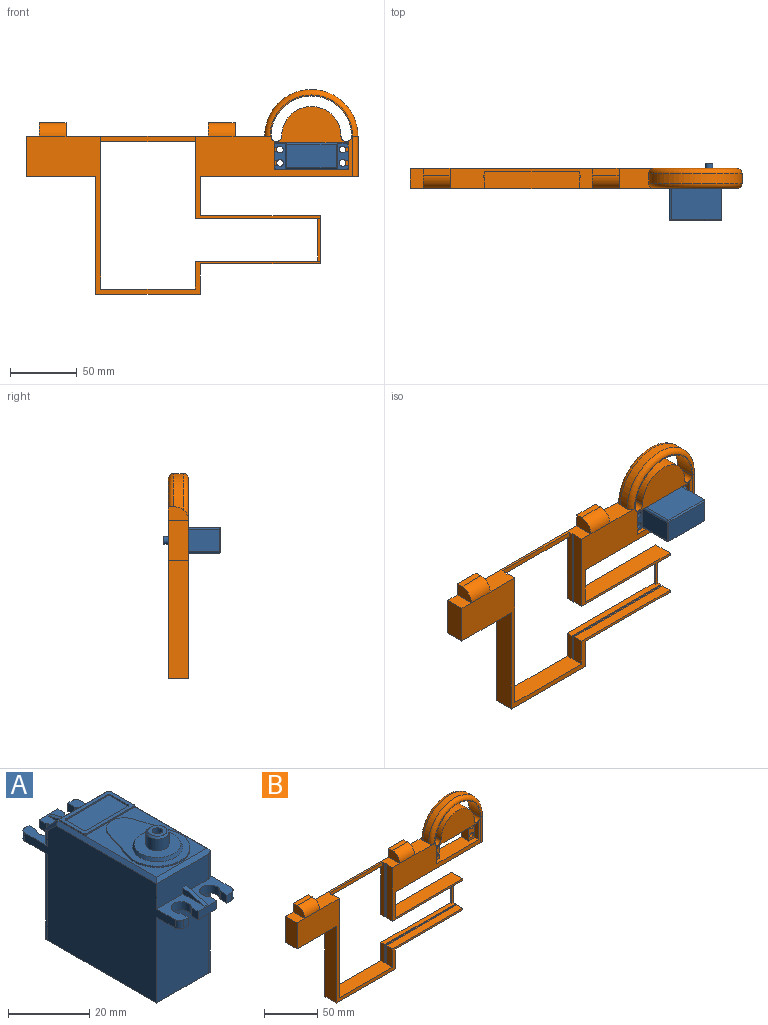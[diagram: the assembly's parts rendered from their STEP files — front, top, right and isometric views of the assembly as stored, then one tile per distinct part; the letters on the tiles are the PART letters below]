
ASSEMBLY  parts=2 mates=1
PART A: 88 faces, bbox 19.5x55.4x43.3 mm
  f0: plane 25.45x17.5mm, normal (0,0,1), area 153.9mm2, adj f42,f43,f44,f45,f56,f57,f58,f77
  f1: plane 17.5x0.91mm, normal (0,0,1), area 7.4mm2, adj f41,f56,f58,f71,f84,f85
  f2: plane 19.5x9.5mm, normal (0,0,1), area 94.3mm2, adj f3,f4,f5,f14,f15,f29,f30,f31
  f3: plane 16.5x3.98mm, normal (0,1,0), area 63.2mm2, adj f2,f36,f37,f38,f60,f61,f62
  f4: plane 2.45x1.5mm, normal (0,1,0), area 3.7mm2, adj f2,f6,f34,f40
  f5: plane 6.5x2.45mm, normal (0,1,0), area 15.9mm2, adj f2,f6,f30,f33
  f6: plane 19.5x9.5mm, normal (0,0,-1), area 103.3mm2, adj f4,f5,f7,f14,f15,f29,f30,f31
  f7: plane 25.85x16.5mm, normal (0,1,0), area 426.5mm2, adj f6,f52,f64,f65
  f8: plane 19.5x9.5mm, normal (0,0,1), area 93.8mm2, adj f9,f10,f11,f14,f15,f17,f18,f19
  f9: plane 18x7.6mm, normal (0,-1,0), area 134.4mm2, adj f8,f14,f24,f25,f26,f57,f63
  f10: plane 6.5x2.45mm, normal (0,-1,0), area 15.9mm2, adj f8,f12,f18,f23
  f11: plane 2.45x1.5mm, normal (0,-1,0), area 3.7mm2, adj f8,f12,f20,f27
  f12: plane 19.5x9.5mm, normal (0,0,-1), area 102.8mm2, adj f10,f11,f13,f14,f15,f17,f18,f19
  f13: plane 25.85x18mm, normal (0,-1,0), area 465.3mm2, adj f12,f14,f53,f66
  f14: plane 52.4x35.9mm, normal (-1,0,0), area 1391.9mm2, adj f2,f6,f8,f9,f12,f13,f27,f39
  f15: plane 52.4x35.9mm, normal (1,0,0), area 1341.7mm2, adj f2,f6,f8,f12,f28,f40,f54,f58
  f16: plane 37.4x17.5mm, normal (0,0,-1), area 654.5mm2, adj f51,f52,f53,f54
  f17: plane 2.45x1.5mm, normal (0,-1,0), area 3.7mm2, adj f8,f12,f21,f28
  f18: plane 2.45x2.41mm, normal (-1,0,0), area 5.9mm2, adj f8,f10,f12,f19
  f19: cylinder r=2.5mm len=5mm, axis (0,0,1), area 29mm2, adj f8,f12,f18,f20
  f20: plane 2.45x2.41mm, normal (1,0,0), area 5.9mm2, adj f8,f11,f12,f19
  f21: plane 2.45x2.41mm, normal (-1,0,0), area 5.9mm2, adj f8,f12,f17,f22
  f22: cylinder r=2.5mm len=5mm, axis (0,0,1), area 29mm2, adj f8,f12,f21,f23
  f23: plane 2.45x2.41mm, normal (1,0,0), area 5.9mm2, adj f8,f10,f12,f22
  f24: plane 7.5x2mm, normal (0,-0.26,0.97), area 9.3mm2, adj f8,f9,f25,f26
  f25: plane 7.5x2mm, normal (1,0,0), area 7.5mm2, adj f8,f9,f24
  f26: plane 7.5x2mm, normal (-1,0,0), area 7.5mm2, adj f8,f9,f24
  f27: cylinder r=1.5mm len=2.45mm, axis (0,0,1), area 5.8mm2, adj f8,f11,f12,f14
  f28: cylinder r=1.5mm len=2.45mm, axis (0,0,-1), area 5.8mm2, adj f8,f12,f15,f17
  f29: plane 2.45x1.5mm, normal (0,1,0), area 3.7mm2, adj f2,f6,f31,f39
  f30: plane 2.45x2.41mm, normal (-1,0,0), area 5.9mm2, adj f2,f5,f6,f32
  f31: plane 2.45x2.41mm, normal (1,0,0), area 5.9mm2, adj f2,f6,f29,f32
  f32: cylinder r=2.5mm len=5mm, axis (0,0,1), area 29mm2, adj f2,f6,f30,f31
  f33: plane 2.45x2.41mm, normal (1,0,0), area 5.9mm2, adj f2,f5,f6,f35
  f34: plane 2.45x2.41mm, normal (-1,0,0), area 5.9mm2, adj f2,f4,f6,f35
  f35: cylinder r=2.5mm len=5mm, axis (0,0,1), area 29mm2, adj f2,f6,f33,f34
  f36: plane 7.5x2mm, normal (0,0.26,0.97), area 9.3mm2, adj f2,f3,f37,f38
  f37: plane 7.5x2mm, normal (1,0,0), area 7.5mm2, adj f2,f3,f36
  f38: plane 7.5x2mm, normal (-1,0,0), area 7.5mm2, adj f2,f3,f36
  f39: cylinder r=1.5mm len=2.45mm, axis (0,0,1), area 5.8mm2, adj f2,f6,f14,f29
  f40: cylinder r=1.5mm len=2.45mm, axis (0,0,-1), area 5.8mm2, adj f2,f4,f6,f15
  f41: plane 17.5x3.56mm, normal (0,0.71,0.71), area 88.1mm2, adj f1,f55,f59,f62
  f42: cylinder r=4.5mm len=8.57mm, axis (0,0,-1), area 4.5mm2, adj f0,f43,f45,f46
  f43: plane 10.43x3.33mm, normal (-0.95,0.3,0), area 4.4mm2, adj f0,f42,f44,f46
  f44: cylinder r=8mm len=16mm, axis (0,0,-1), area 12mm2, adj f0,f43,f45,f46
  f45: plane 10.43x3.33mm, normal (0.95,0.3,0), area 4.4mm2, adj f0,f42,f44,f46
  f46: plane 24x16mm, normal (0,0,1), area 164mm2, adj f42,f43,f44,f45,f48
  f47: plane 11.5x11.5mm, normal (0,0,1), area 78.4mm2, adj f48,f49
  f48: cone r=6.15mm half-angle=21.8deg, axis (0,0,-1), area 40.3mm2, adj f46,f47
  f49: cylinder r=2.85mm len=5.7mm, axis (0,0,-1), area 62.7mm2, adj f47,f67
  f50: plane 4.7x4.7mm, normal (0,0,1), area 12.4mm2, adj f67,f68
  f51: plane 38.96x1mm, normal (-0.71,0,-0.71), area 54mm2, adj f14,f16,f52,f53,f65
  f52: plane 18.62x1mm, normal (0,0.71,-0.71), area 25.5mm2, adj f7,f16,f51,f54,f64,f65
  f53: plane 19.06x1mm, normal (0,-0.71,-0.71), area 25.8mm2, adj f13,f16,f51,f54,f66
  f54: plane 38.52x1mm, normal (0.71,0,-0.71), area 53.6mm2, adj f15,f16,f52,f53,f64,f66
  f55: plane 4.39x4.29mm, normal (-0.71,0.5,0.5), area 7.5mm2, adj f14,f41,f56,f60,f62
  f56: plane 35.4x1mm, normal (-0.71,0,0.71), area 49.1mm2, adj f0,f1,f14,f55,f57,f72
  f57: plane 19.06x1mm, normal (0,-0.71,0.71), area 25.8mm2, adj f0,f9,f56,f58,f63
  f58: plane 34.96x1mm, normal (0.71,0,0.71), area 48.7mm2, adj f0,f1,f15,f57,f59,f63,f70
  f59: plane 4.39x4.29mm, normal (0.71,0.5,0.5), area 7.5mm2, adj f15,f41,f58,f61,f62
  f60: cylinder r=1.5mm len=4.69mm, axis (0,0,1), area 10.2mm2, adj f2,f3,f14,f55,f62
  f61: cylinder r=1.5mm len=4.69mm, axis (0,0,-1), area 10.2mm2, adj f2,f3,f15,f59,f62
  f62: cylinder r=1.5mm len=17.71mm, axis (-1,0,0), area 20.4mm2, adj f3,f41,f55,f59,f60,f61
  f63: cylinder r=1.5mm len=8.04mm, axis (0,0,1), area 18.3mm2, adj f8,f9,f15,f57,f58
  f64: cylinder r=1.5mm len=26.29mm, axis (0,0,-1), area 61.3mm2, adj f6,f7,f15,f52,f54
  f65: cylinder r=1.5mm len=26.29mm, axis (0,0,1), area 61.3mm2, adj f6,f7,f14,f51,f52
  f66: cylinder r=1.5mm len=26.29mm, axis (0,0,1), area 61.3mm2, adj f12,f13,f15,f53,f54
  f67: cone r=2.35mm half-angle=45deg, axis (0,0,-1), area 11.6mm2, adj f49,f50
  f68: cylinder r=1.25mm len=8mm, axis (0,0,1), area 62.8mm2, adj f50,f69
  f69: plane 2.5x2.5mm, normal (0,0,1), area 4.9mm2, adj f68
  f70: plane 8.04x0.4mm, normal (1,0,0), area 3.2mm2, adj f58,f78,f84,f87
  f71: plane 16.5x0.4mm, normal (0,1,0), area 6.6mm2, adj f1,f78,f84,f85
  f72: plane 8.04x0.4mm, normal (-1,0,0), area 3.2mm2, adj f56,f78,f85,f86
  f73: plane 14.5x0.4mm, normal (0,-1,0), area 5.8mm2, adj f78,f79,f80,f83
  f74: plane 6.04x0.4mm, normal (-1,0,0), area 2.4mm2, adj f78,f79,f80,f81
  f75: plane 14.5x0.4mm, normal (0,1,0), area 5.8mm2, adj f78,f79,f81,f82
  f76: plane 6.04x0.4mm, normal (1,0,0), area 2.4mm2, adj f78,f79,f82,f83
  f77: plane 16.5x0.4mm, normal (0,-1,0), area 6.6mm2, adj f0,f78,f86,f87
  f78: plane 17.5x9.04mm, normal (0,0,1), area 49.1mm2, adj f70,f71,f72,f73,f74,f75,f76,f77
  f79: plane 15.5x7.04mm, normal (0,0,1), area 108.8mm2, adj f73,f74,f75,f76,f80,f81,f82,f83
  f80: cylinder r=0.5mm len=0.5mm, axis (0,0,-1), area 0.3mm2, adj f73,f74,f78,f79
  f81: cylinder r=0.5mm len=0.5mm, axis (0,0,1), area 0.3mm2, adj f74,f75,f78,f79
  f82: cylinder r=0.5mm len=0.5mm, axis (0,0,-1), area 0.3mm2, adj f75,f76,f78,f79
  f83: cylinder r=0.5mm len=0.5mm, axis (0,0,1), area 0.3mm2, adj f73,f76,f78,f79
  f84: cylinder r=0.5mm len=0.5mm, axis (0,0,-1), area 0.3mm2, adj f1,f70,f71,f78
  f85: cylinder r=0.5mm len=0.5mm, axis (0,0,-1), area 0.3mm2, adj f1,f71,f72,f78
  f86: cylinder r=0.5mm len=0.5mm, axis (0,0,1), area 0.3mm2, adj f0,f72,f77,f78
  f87: cylinder r=0.5mm len=0.5mm, axis (0,0,1), area 0.3mm2, adj f0,f70,f77,f78
PART B: 72 faces, bbox 251.9x15x156.5 mm
  f0: plane 26.2x15mm, normal (0,0,1), area 339.9mm2, adj f1,f13,f27,f45,f47,f68
  f1: plane 118.2x92.6mm, normal (0,-1,0), area 3548.4mm2, adj f0,f2,f10,f16,f24,f25,f31,f32
  f2: plane 106.8x15mm, normal (0,0,1), area 680.2mm2, adj f1,f3,f11,f13,f15,f16,f19,f20
  f3: plane 220.8x118.6mm, normal (0,-1,0), area 2602.8mm2, adj f2,f4,f10,f14,f15,f21,f22,f23
  f4: plane 21x8mm, normal (-1,0,0), area 168mm2, adj f3,f6,f30,f62
  f5: plane 21x5mm, normal (-1,0,0), area 105mm2, adj f7,f8,f13,f30
  f6: plane 94x21mm, normal (0,1,0), area 114mm2, adj f4,f10,f30,f58,f62,f66
  f7: plane 94x21mm, normal (0,-1,0), area 114mm2, adj f5,f8,f10,f30,f58,f66
  f8: plane 94x5mm, normal (0,0,1), area 466mm2, adj f5,f7,f10,f12,f13,f64
  f9: plane 94x5mm, normal (0,0,-1), area 466mm2, adj f10,f12,f13,f20,f59,f64
  f10: plane 36x15mm, normal (1,0,0), area 120mm2, adj f1,f3,f6,f7,f8,f9,f13,f57
  f11: plane 60.6x2mm, normal (-1,0,0), area 121.2mm2, adj f2,f57,f59,f65
  f12: plane 32x2mm, normal (-1,0,0), area 64mm2, adj f8,f9,f13,f64
  f13: plane 245x149.6mm, normal (0,1,0), area 7139.1mm2, adj f0,f2,f5,f8,f9,f10,f12,f14
  f14: plane 23x15mm, normal (1,0,0), area 345mm2, adj f3,f13,f23,f61
  f15: plane 114.6x8mm, normal (1,0,0), area 916.8mm2, adj f2,f3,f30,f56
  f16: plane 61.6x8mm, normal (-1,0,0), area 492.8mm2, adj f1,f2,f57,f63
  f17: plane 70.6x2mm, normal (0,0,-1), area 141.2mm2, adj f13,f19,f20,f53
  f18: plane 20x8mm, normal (0,-1,0), area 120.7mm2, adj f35,f36,f38,f40,f51,f52
  f19: plane 114.6x5mm, normal (1,0,0), area 565mm2, adj f2,f13,f17,f30,f53,f54
  f20: plane 61.6x5mm, normal (-1,0,0), area 300mm2, adj f2,f9,f13,f17,f53,f59
  f21: plane 52.2x15mm, normal (0,0,-1), area 783mm2, adj f3,f13,f22,f29
  f22: plane 88.6x15mm, normal (-1,0,0), area 1329mm2, adj f3,f13,f21,f23
  f23: plane 78.6x15mm, normal (0,0,-1), area 1179mm2, adj f3,f13,f14,f22
  f24: plane 29.6x15mm, normal (1,0,0), area 444mm2, adj f1,f13,f25,f60
  f25: plane 118.2x15mm, normal (0,0,-1), area 1766.1mm2, adj f1,f13,f24,f26,f46,f48
  f26: plane 30x7mm, normal (1,0,0), area 210mm2, adj f25,f27,f46,f48
  f27: cylinder r=35mm len=70mm, axis (0,1,0), area 769.7mm2, adj f0,f26,f45,f47
  f28: plane 15x10mm, normal (0,0,1), area 150mm2, adj f3,f13,f29,f43
  f29: plane 30x15mm, normal (-1,0,0), area 450mm2, adj f3,f13,f21,f28
  f30: plane 72.6x15mm, normal (0,0,1), area 1063mm2, adj f3,f4,f5,f6,f7,f13,f15,f19
  f31: cylinder r=22.25mm len=44.5mm, axis (0,-1,0), area 1051.5mm2, adj f1,f13,f32,f34
  f32: cylinder r=4mm len=15mm, axis (0,-1,0), area 188.5mm2, adj f1,f13,f31,f33
  f33: cylinder r=30.25mm len=60.5mm, axis (0,-1,0), area 1425.5mm2, adj f1,f13,f32,f34
  f34: cylinder r=4mm len=15mm, axis (0,-1,0), area 188.5mm2, adj f1,f13,f31,f33
  f35: plane 20x5mm, normal (-1,0,0), area 100mm2, adj f1,f18,f36,f38
  f36: plane 55.4x15mm, normal (0,0,-1), area 671mm2, adj f1,f13,f18,f35,f37,f39,f40,f41
  f37: plane 20x5mm, normal (1,0,0), area 100mm2, adj f1,f36,f38,f39
  f38: plane 55.4x15mm, normal (0,0,1), area 671mm2, adj f1,f13,f18,f35,f37,f39,f40,f41
  f39: plane 20x8mm, normal (0,-1,0), area 120.7mm2, adj f36,f37,f38,f41,f49,f50
  f40: plane 20x10mm, normal (-1,0,0), area 200mm2, adj f13,f18,f36,f38
  f41: plane 20x10mm, normal (1,0,0), area 200mm2, adj f13,f36,f38,f39
  f42: plane 15x10mm, normal (1,0,0), area 128.5mm2, adj f2,f13,f44,f67
  f43: plane 15x10mm, normal (-1,0,0), area 128.5mm2, adj f13,f28,f44,f67
  f44: plane 20x5mm, normal (0,0,1), area 100mm2, adj f13,f42,f43,f67
  f45: torus R=31mm, axis (0,-1,0), area 662.2mm2, adj f0,f1,f27,f46
  f46: cylinder r=4mm len=30mm, axis (0,0,-1), area 188.5mm2, adj f1,f25,f26,f45
  f47: torus R=31mm, axis (0,-1,0), area 662.2mm2, adj f0,f13,f27,f48
  f48: cylinder r=4mm len=30mm, axis (0,0,1), area 188.5mm2, adj f13,f25,f26,f47
  f49: cylinder r=2.5mm len=10mm, axis (0,-1,0), area 157.1mm2, adj f13,f39
  f50: cylinder r=2.5mm len=10mm, axis (0,-1,0), area 157.1mm2, adj f13,f39
  f51: cylinder r=2.5mm len=10mm, axis (0,-1,0), area 157.1mm2, adj f13,f18
  f52: cylinder r=2.5mm len=10mm, axis (0,-1,0), area 157.1mm2, adj f13,f18
  f53: plane 70.6x4mm, normal (0,-1,0), area 282.4mm2, adj f2,f17,f19,f20
  f54: plane 114.6x1mm, normal (0,-1,0), area 114.6mm2, adj f2,f19,f30,f55
  f55: plane 114.6x2mm, normal (1,0,0), area 229.2mm2, adj f2,f30,f54,f56
  f56: plane 114.6x1mm, normal (0,1,0), area 114.6mm2, adj f2,f15,f30,f55
  f57: plane 94x61.6mm, normal (0,1,0), area 154.6mm2, adj f2,f10,f11,f16,f63,f65
  f58: plane 20x2mm, normal (-1,0,0), area 40mm2, adj f6,f7,f30,f66
  f59: plane 94x61.6mm, normal (0,-1,0), area 154.6mm2, adj f2,f9,f10,f11,f20,f65
  f60: plane 90x15mm, normal (0,0,1), area 1350mm2, adj f1,f10,f13,f24
  f61: plane 90x15mm, normal (0,0,-1), area 1350mm2, adj f3,f10,f13,f14
  f62: plane 94x8mm, normal (0,0,1), area 752mm2, adj f3,f4,f6,f10
  f63: plane 94x8mm, normal (0,0,-1), area 752mm2, adj f1,f10,f16,f57
  f64: plane 32x2mm, normal (0,-1,0), area 64mm2, adj f8,f9,f10,f12
  f65: plane 93x2mm, normal (0,0,-1), area 186mm2, adj f10,f11,f57,f59
  f66: plane 93x2mm, normal (0,0,1), area 186mm2, adj f6,f7,f10,f58
  f67: cylinder r=10mm len=20mm, axis (-1,0,0), area 314.2mm2, adj f3,f42,f43,f44
  f68: plane 15x10mm, normal (1,0,0), area 128.5mm2, adj f0,f13,f70,f71
  f69: plane 15x10mm, normal (-1,0,0), area 128.5mm2, adj f2,f13,f70,f71
  f70: plane 20x5mm, normal (0,0,1), area 100mm2, adj f13,f68,f69,f71
  f71: cylinder r=10mm len=20mm, axis (-1,0,0), area 314.2mm2, adj f1,f68,f69,f70
PLACE A rot(axis=(-0.58,0.58,0.58),120deg) t=(54.99,-31.43,6.59)mm
PLACE B t=(-69.51,7.87,6.59)mm
MATE fastened A.f22 <-> B.f51  axis (0,1,0) through (78.49,-2.13,1.59)mm
